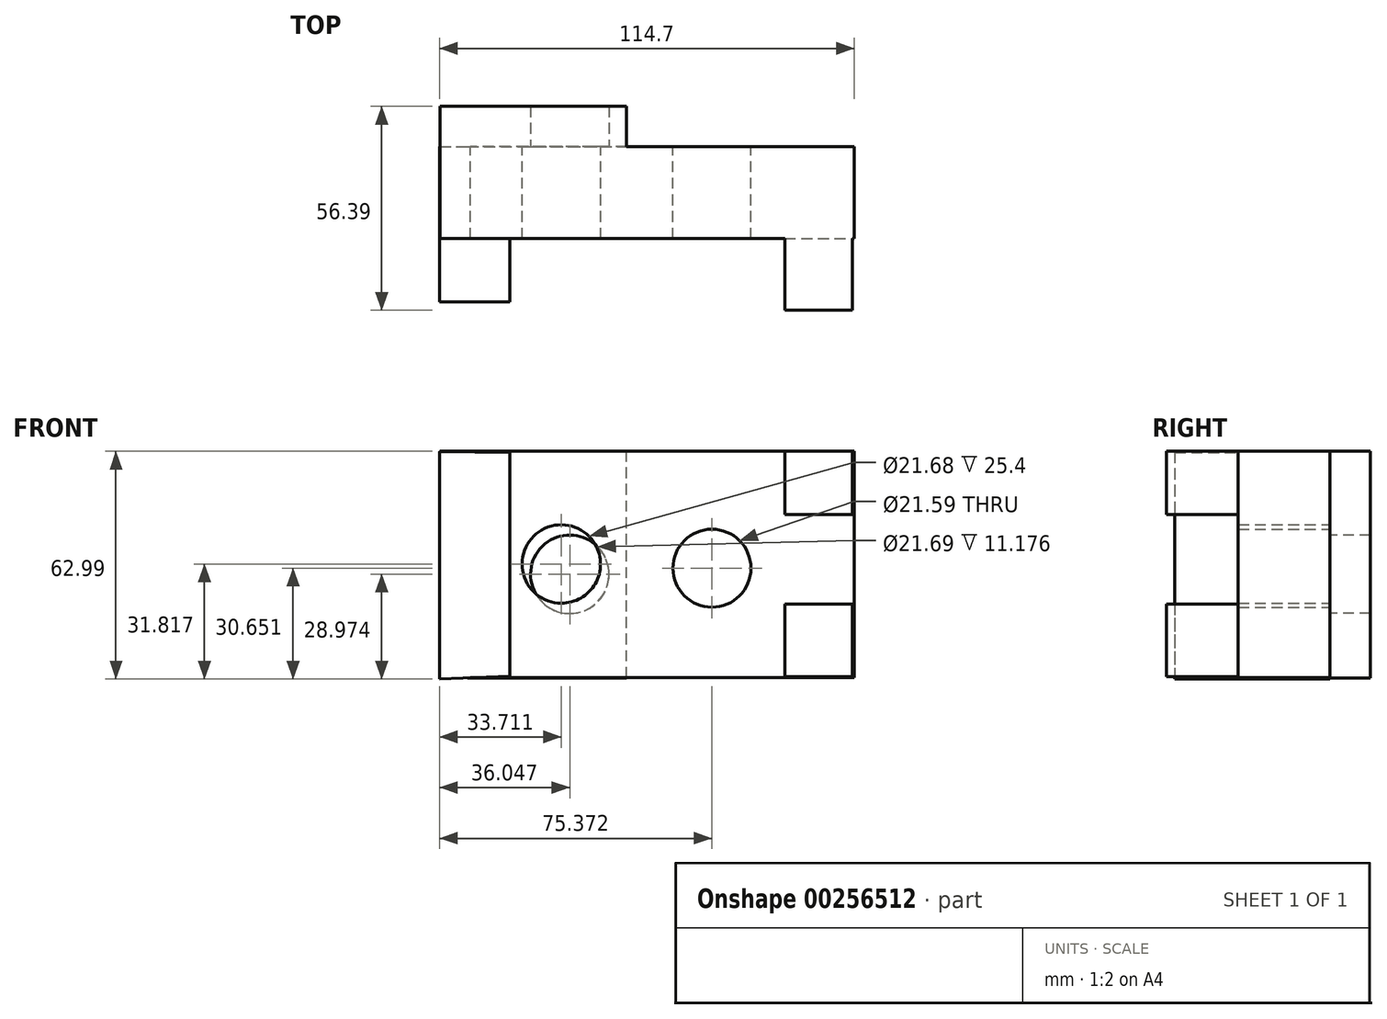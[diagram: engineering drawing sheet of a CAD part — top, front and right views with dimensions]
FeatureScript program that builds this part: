
annotation { "Feature Type Name" : "Feature", "Feature Type Description" : "" }
export const myFeature = defineFeature(function(context is Context, id is Id, definition is map)
    precondition{}
    {
        {
            var Q0;
            Q0=qCreatedBy(makeId("Front.planeOp"),FACE);
            var sketch = newSketch(context, id + "F0", { "sketchPlane" : qUnion([Q0])});
            skLineSegment(sketch, "E0", {"start": v(-62.07, 36.58) * mm, "end": v(52.42, 36.58) * mm});
            skLineSegment(sketch, "E1", {"start": v(52.42, 36.58) * mm, "end": v(52.42, -26.06) * mm});
            skLineSegment(sketch, "E2", {"start": v(52.42, -26.06) * mm, "end": v(-62.07, -26.06) * mm});
            skLineSegment(sketch, "E3", {"start": v(-62.07, -26.06) * mm, "end": v(-62.07, 36.58) * mm});
            skSolve(sketch);
        }
        {
            var Q0;
            Q0 = qSketchRegion(id + "F0", true);
            extrude(context, id + "F1", {"entities" : qUnion([Q0]), "depth" : 25.4 * mm});
        }
        {
            var Q0;
            Q0=qCreatedBy(makeId("Front.planeOp"),FACE);
            var sketch = newSketch(context, id + "F2", { "sketchPlane" : qUnion([Q0])});
            skCircle(sketch, "E4", {"center": v(13.1, 4.24) * mm, "radius": 10.8 * mm});
            skCircle(sketch, "E5", {"center": v(-28.57, 5.4) * mm, "radius": 10.8 * mm});
            skCircle(sketch, "E6", {"center": v(-28.57, 5.4) * mm, "radius": 10.84 * mm});
            skSolve(sketch);
        }
        {
            var Q0;
            Q0 = qSketchRegion(id + "F2", true);
            var Q1;
            Q1=makeQuery(id+"F2.imprint","IMPRINT",FACE,{"disambiguationData":[TD([[makeQuery(id+"F2.imprint","IMPRINT",EDGE,{"derivedFrom":sQuery(id+"F2.wireOp",EDGE,"E5")}),1.0]])]});
            extrude(context, id + "F3", {"entities" : qUnion([Q0, Q1]), "operationType" : NewBodyOperationType.REMOVE, "depth" : 116.84 * mm});
        }
        {
            var Q0;
            Q0=qCreatedBy(makeId("Front.planeOp"),FACE);
            var sketch = newSketch(context, id + "F4", { "sketchPlane" : qUnion([Q0])});
            skLineSegment(sketch, "E7", {"start": v(-42.86, 36.29) * mm, "end": v(-42.86, -25.6) * mm});
            skLineSegment(sketch, "E8", {"start": v(-62.28, -26.4) * mm, "end": v(-42.86, -25.6) * mm});
            skLineSegment(sketch, "E9", {"start": v(-62.28, 36.47) * mm, "end": v(-62.28, -26.4) * mm});
            skLineSegment(sketch, "E10", {"start": v(-42.86, 36.29) * mm, "end": v(-62.28, 36.47) * mm});
            skSolve(sketch);
        }
        {
            var Q0;
            Q0 = qSketchRegion(id + "F4", true);
            extrude(context, id + "F5", {"entities" : qUnion([Q0]), "operationType" : NewBodyOperationType.ADD, "depth" : 42.93 * mm});
        }
        {
            var Q0;
            Q0=qCreatedBy(makeId("Front.planeOp"),FACE);
            var sketch = newSketch(context, id + "F6", { "sketchPlane" : qUnion([Q0])});
            skLineSegment(sketch, "E11", {"start": v(-62.08, -26.09) * mm, "end": v(-10.5, -26.09) * mm});
            skLineSegment(sketch, "E12", {"start": v(-10.5, -26.09) * mm, "end": v(-10.5, 36.58) * mm});
            skLineSegment(sketch, "E13", {"start": v(-10.5, 36.58) * mm, "end": v(-62.08, 36.58) * mm});
            skLineSegment(sketch, "E14", {"start": v(-62.08, 36.58) * mm, "end": v(-62.08, -26.09) * mm});
            skSolve(sketch);
        }
        {
            var Q0;
            Q0 = qSketchRegion(id + "F6", true);
            extrude(context, id + "F7", {"entities" : qUnion([Q0]), "operationType" : NewBodyOperationType.ADD, "oppositeDirection" : true, "depth" : 11.18 * mm});
        }
        {
            var Q0;
            Q0=qCreatedBy(makeId("Front.planeOp"),FACE);
            var sketch = newSketch(context, id + "F8", { "sketchPlane" : qUnion([Q0])});
            skCircle(sketch, "E15", {"center": v(-26.23, 2.56) * mm, "radius": 10.85 * mm});
            skSolve(sketch);
        }
        {
            var Q0;
            Q0 = qSketchRegion(id + "F8", true);
            extrude(context, id + "F9", {"entities" : qUnion([Q0]), "operationType" : NewBodyOperationType.REMOVE, "oppositeDirection" : true, "depth" : 65.53 * mm});
        }
        {
            var Q0;
            Q0=qCreatedBy(makeId("Front.planeOp"),FACE);
            var sketch = newSketch(context, id + "F10", { "sketchPlane" : qUnion([Q0])});
            skLineSegment(sketch, "E16", {"start": v(51.88, -5.68) * mm, "end": v(33.23, -5.68) * mm});
            skLineSegment(sketch, "E17", {"start": v(33.23, -5.68) * mm, "end": v(33.23, -25.8) * mm});
            skLineSegment(sketch, "E18", {"start": v(33.23, 36.58) * mm, "end": v(33.23, 19.1) * mm});
            skLineSegment(sketch, "E19", {"start": v(33.23, 19.1) * mm, "end": v(51.88, 19.1) * mm});
            skLineSegment(sketch, "E20", {"start": v(51.88, 19.1) * mm, "end": v(51.88, 36.58) * mm});
            skLineSegment(sketch, "E21", {"start": v(51.88, 36.58) * mm, "end": v(33.23, 36.58) * mm});
            skLineSegment(sketch, "E22", {"start": v(51.88, -5.68) * mm, "end": v(51.88, -25.8) * mm});
            skLineSegment(sketch, "E23", {"start": v(51.88, -25.8) * mm, "end": v(33.23, -25.8) * mm});
            skLineSegment(sketch, "E24", {"start": v(33.23, -25.8) * mm, "end": v(51.88, -25.8) * mm});
            skSolve(sketch);
        }
        {
            var Q0;
            Q0 = qSketchRegion(id + "F10", true);
            extrude(context, id + "F11", {"entities" : qUnion([Q0]), "operationType" : NewBodyOperationType.ADD, "depth" : 45.2 * mm});
        }
    });
